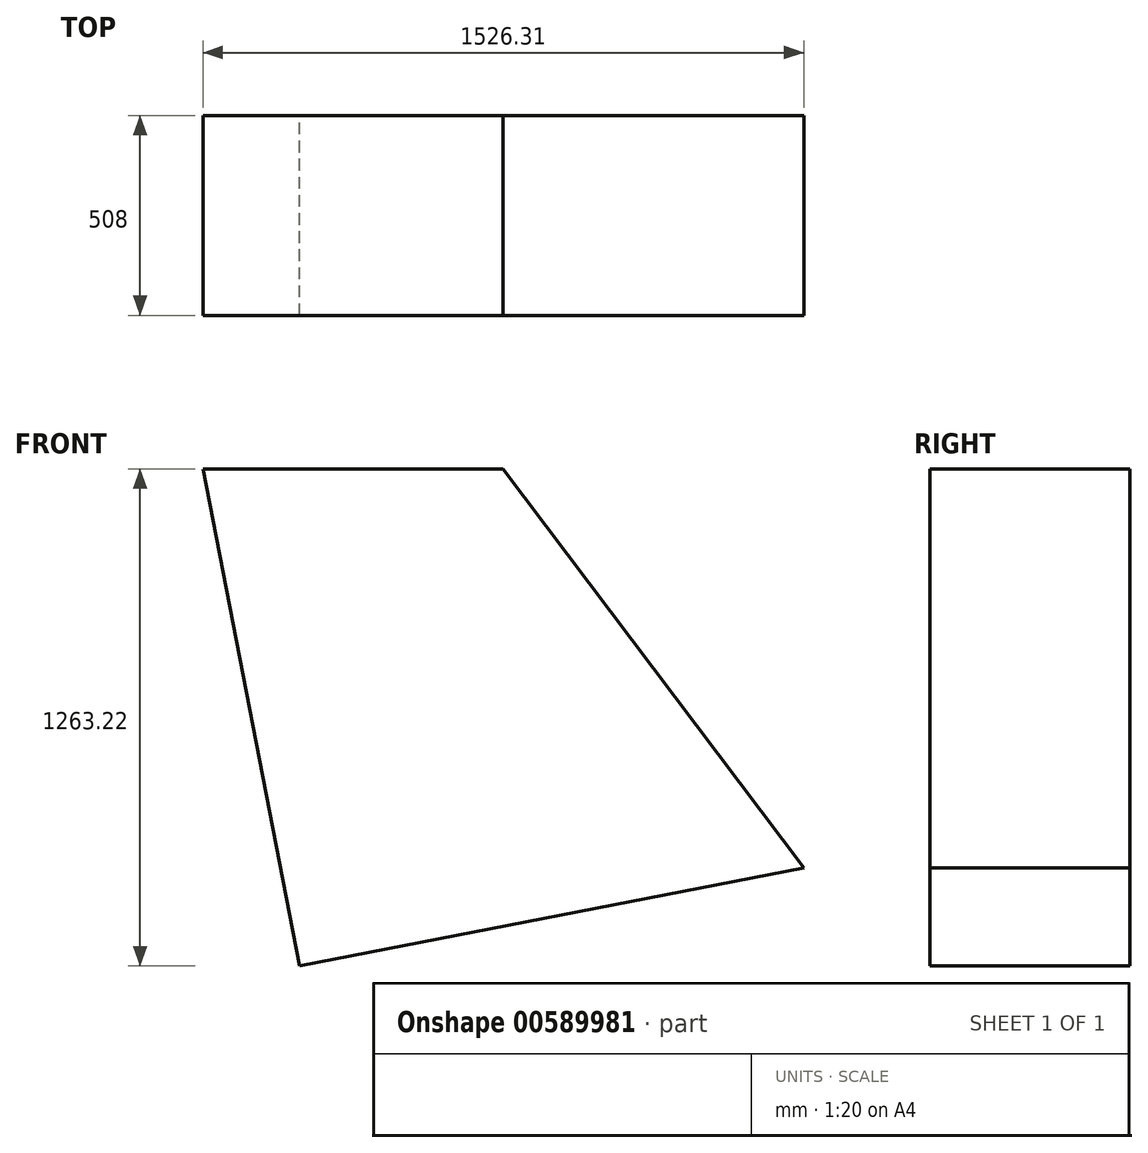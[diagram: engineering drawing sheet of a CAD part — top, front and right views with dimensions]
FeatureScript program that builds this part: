
annotation { "Feature Type Name" : "Feature", "Feature Type Description" : "" }
export const myFeature = defineFeature(function(context is Context, id is Id, definition is map)
    precondition{}
    {
        {
            var Q0;
            Q0=qCreatedBy(makeId("Front.planeOp"),FACE);
            var sketch = newSketch(context, id + "F0", { "sketchPlane" : qUnion([Q0])});
            skLineSegment(sketch, "E0", {"start": v(0, 0) * mm, "end": v(-764.3, 1014.27) * mm});
            skLineSegment(sketch, "E1", {"start": v(-764.3, 1014.27) * mm, "end": v(-1526.3, 1014.27) * mm});
            skLineSegment(sketch, "E2", {"start": v(-1526.3, 1014.27) * mm, "end": v(-1280.76, -248.95) * mm});
            skLineSegment(sketch, "E3", {"start": v(-1280.76, -248.95) * mm, "end": v(0, 0) * mm});
            skSolve(sketch);
        }
        {
            var Q0;
            Q0 = qSketchRegion(id + "F0", true);
            extrude(context, id + "F1", {"entities" : qUnion([Q0]), "depth" : 508 * mm, "offsetDistance" : 25.4 * mm});
        }
    });
